# Revit family: Electronics_Conferencing-Bars_Biamp_Parle_Video_VBC-2500a
name_source: partatom
category: Communication Devices
units: mm (PartAtom-declared; Revit-internal decimal feet)

## family parameters
Cut with Voids When Loaded = No
Host = Face
Maintain Annotation Orientation = No
OmniClass Number = 23.85.10.17.11.14
OmniClass Title = Audio-Visual Recorders (Cam-Corders)
Part Type = Normal
Room Calculation Point = No
Round Connector Dimension = Use Diameter
Shared = No

## types (1)
- Parlé™ VBC 2500a
    Altitude = 0-10,000 ft (0-3000m) MSL
    Apparent Load = 60 VA
    Audio Processing = AEC (Acoustic Echo Cancellation)
    Camera Indicators = Camera Active Indicator (White/Off LED)
    Compliance = FCC Part 15B (USA) CE Marked (Europe) UL and C-UL listed (USA and Canada) RoHS Directive (Europe)
    Connector Description = USB-C
    Default Elevation = 1219.2 mm  [stored 4 ft]
    Depth = 63.5 mm
    Description = Parlé™ VBC 2500a Conferencing Video Bar
    Diagonal Field of View = 120 Degrees
    Digital Zoom = 5x
    Focus Distance Nominal = 100 cm
    Height = 99.06 mm  [stored 0.325 ft]
    Housing Material = Biamp - Plastic - Black
    Humidity = 0-90% relative humidity (non-condensing)
    Image Sensor = 12 Megapixel
    Lens Cap = Automated Privacy Shutter
    Loudspeakers Frequency Response = -10 dB
    Loudspeakers Sensitivity = 84 dB
    Manufacturer = Biamp
    Max Power Consumption = 60 W
    Maximum SPL = 130 dB
    Microphone Data Rate Output = 48 kHz
    Microphone Frequency Response = -10dB
    Microphone Indicators = Mute Indicator (Green/Red/Off LEDs)
    Microphone Sensitivity = > -37dBFS ± 1dB
    Microphone Technology = 27-Element Digital Array
    Model = Parlé™ VBC 2500a
    Noise Reduction = AI filter
    Nominal Beamwidth = 180° x 180°
    Nominal Impedance = 4 ohm
    Number of Poles = 1
    Pickup Range = > 23 feet (7 m)
    Polar Pattern = Active Beamformed
    Positioning = Autoframing capability Electronic Pan/Tilt/Zoom UVC controlled
    Power Factor = 1
    Product Documentation Link = https://downloads.biamp.com
    Product Page URL = https://www.biamp.com
    Product data url = https://www.bimobject.com
    Rated Maximum SPL = 90 dB (continuous)
    SNR = 69 dB
    Sampling Rate = 48 kHz
    Supported Video Resolutions = 720p at 30fps; 1080p at 30fps; 2160p at 30fps
    THD = < 0.2%
    Temperature Range = 32 - 104° F (0 - 40° C)
    Transducers = 2x 2.5 in (60 mm) full range
    URL = https://www.biamp.com
    USB 3.0 = 1x Type C
    Version = 1
    Voltage = 0 V
    Weight = 9.60 lbf
    Width = 939.8 mm  [stored 3.08333 ft]

note: [stored X ft] marks values corroborated as IEEE doubles in the binary element streams (Revit-internal decimal feet)

## geometry (parser evidence)
native form markers: Sweep x10
no freeform markers — native parametric forms only
